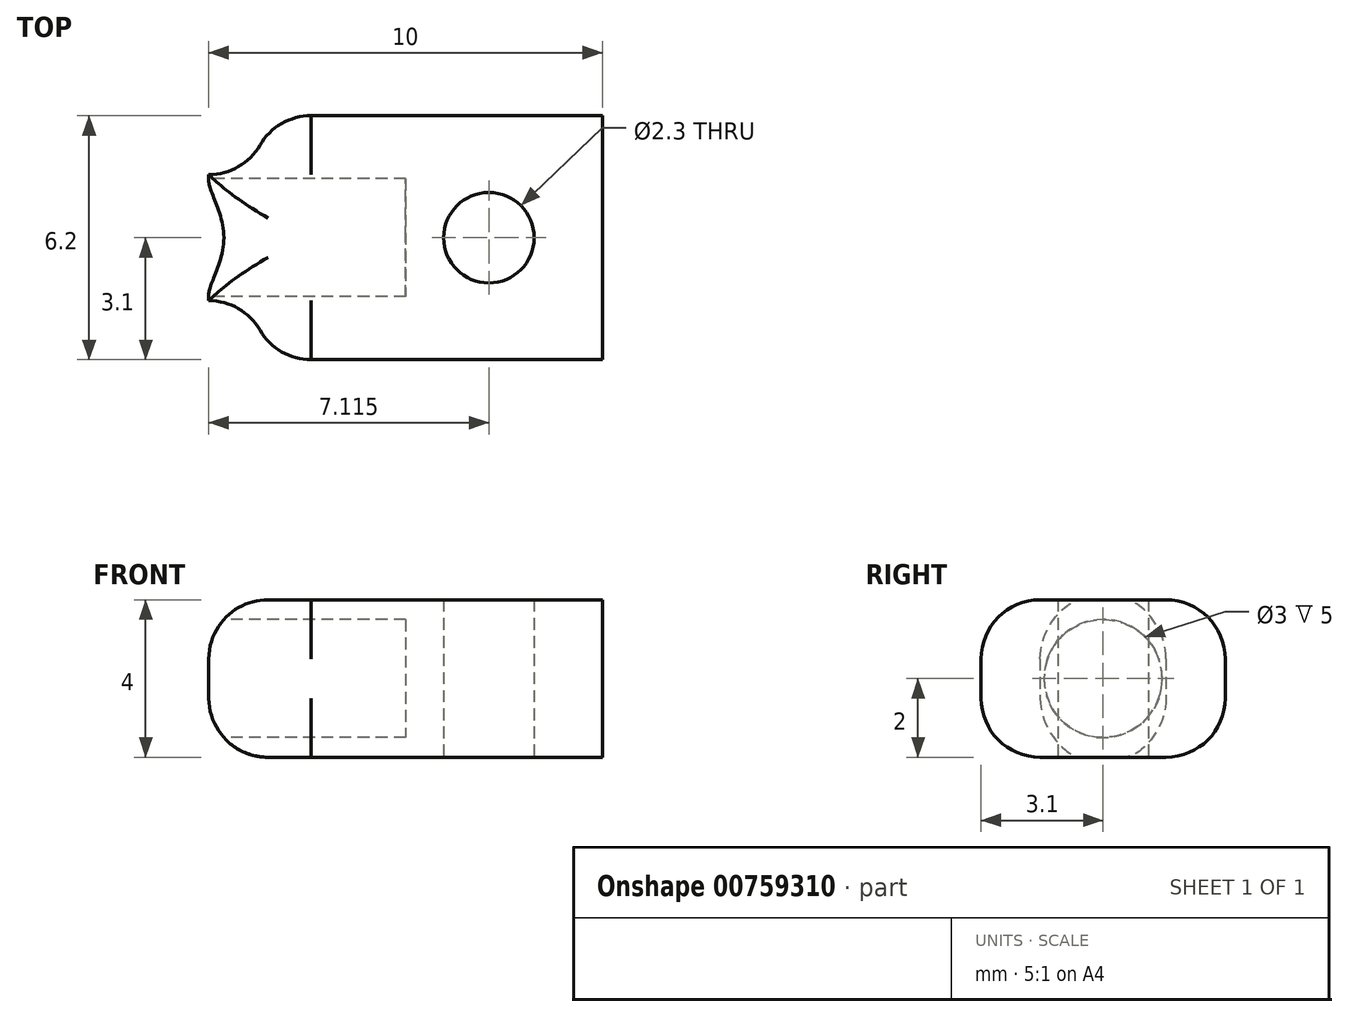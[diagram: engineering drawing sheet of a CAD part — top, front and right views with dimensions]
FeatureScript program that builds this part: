
annotation { "Feature Type Name" : "Feature", "Feature Type Description" : "" }
export const myFeature = defineFeature(function(context is Context, id is Id, definition is map)
    precondition{}
    {
        {
            var Q0;
            Q0=qCreatedBy(makeId("Top.planeOp"),FACE);
            var sketch = newSketch(context, id + "F0", { "sketchPlane" : qUnion([Q0])});
            skLineSegment(sketch, "E0.bottom", {"start": v(-3.5, 3.1) * mm, "end": v(5, 3.1) * mm});
            skLineSegment(sketch, "E0.top", {"start": v(-3.5, -3.1) * mm, "end": v(5, -3.1) * mm});
            skLineSegment(sketch, "E0.left", {"start": v(-5, 1.6) * mm, "end": v(-5, -1.6) * mm});
            skLineSegment(sketch, "E0.right", {"start": v(5, 3.1) * mm, "end": v(5, -3.1) * mm});
            skPoint(sketch, "E0.middle", {"position": v(0, 0) * mm});
            skArc(sketch, "E1", {"start": v(-3.5, -3.1) * mm, "mid": v(-3.94, -2.04) * mm, "end": v(-5, -1.6) * mm});
            skArc(sketch, "E2", {"start": v(-5, 1.6) * mm, "mid": v(-3.94, 2.04) * mm, "end": v(-3.5, 3.1) * mm});
            skLineSegment(sketch, "E3", {"start": v(0.97, 0) * mm, "end": v(1.15, 0) * mm});
            skCircle(sketch, "E4", {"center": v(2.12, 0) * mm, "radius": 1.15 * mm});
            skSolve(sketch);
        }
        {
            var Q0;
            Q0 = qSketchRegion(id + "F0", true);
            extrude(context, id + "F1", {"entities" : qUnion([Q0]), "depth" : 4 * mm, "offsetDistance" : 25 * mm});
        }
        {
            var Q0;
            Q0=makeQuery(id+"F1.opExtrude","SWEPT_FACE",FACE,{"disambiguationData":[OSD([sQuery(id+"F0.wireOp",EDGE,"E0.left")])]});
            var sketch = newSketch(context, id + "F2", { "sketchPlane" : qUnion([Q0])});
            skCircle(sketch, "E5", {"center": v(0, 2) * mm, "radius": 1.5 * mm});
            skPoint(sketch, "E6.trimOffspring.end.orphan", {"position": v(0, 4) * mm});
            skPoint(sketch, "E7.start.orphan", {"position": v(-1.6, 2) * mm});
            skPoint(sketch, "E8.trimOffspring.end.orphan", {"position": v(1.6, 2) * mm});
            skSolve(sketch);
        }
        {
            var Q0;
            Q0=makeQuery(id+"F2.imprint","IMPRINT",FACE,{"disambiguationData":[TD([[makeQuery(id+"F2.imprint","IMPRINT",EDGE,{"derivedFrom":sQuery(id+"F2.wireOp",EDGE,"E5")}),1.0]])]});
            extrude(context, id + "F3", {"entities" : qUnion([Q0]), "operationType" : NewBodyOperationType.REMOVE, "oppositeDirection" : true, "depth" : 5 * mm, "offsetDistance" : 25 * mm});
        }
        {
            var Q0;
            Q0=makeQuery(id+"F1.opExtrude","CAP_EDGE",EDGE,{"disambiguationData":[OSD([sQuery(id+"F0.wireOp",EDGE,"E0.top")])],"isStart":false});
            var Q1;
            Q1=makeQuery(id+"F1.opExtrude","CAP_EDGE",EDGE,{"disambiguationData":[OSD([sQuery(id+"F0.wireOp",EDGE,"E0.top")])],"isStart":true});
            var Q2;
            Q2=makeQuery(id+"F1.opExtrude","CAP_EDGE",EDGE,{"disambiguationData":[OSD([sQuery(id+"F0.wireOp",EDGE,"E0.bottom")])],"isStart":false});
            var Q3;
            Q3=makeQuery(id+"F1.opExtrude","CAP_EDGE",EDGE,{"disambiguationData":[OSD([sQuery(id+"F0.wireOp",EDGE,"E0.bottom")])],"isStart":true});
            fillet(context, id + "F4", {"entities" : qUnion([Q0, Q1, Q2, Q3]), "radius" : 1.5 * mm, "tangentPropagation" : true, "allowEdgeOverflow" : false});
        }
        {
            var Q0;
            Q0=makeQuery(id+"F1.opExtrude","CAP_EDGE",EDGE,{"disambiguationData":[OSD([sQuery(id+"F0.wireOp",EDGE,"E0.left")])],"isStart":false});
            var Q1;
            Q1=makeQuery(id+"F1.opExtrude","CAP_EDGE",EDGE,{"disambiguationData":[OSD([sQuery(id+"F0.wireOp",EDGE,"E0.left")])],"isStart":true});
            var Q2;
            Q2=makeQuery(id+"F4.opFillet","BLEND_EDGE",EDGE,{"blendedFrom":[makeQuery(id+"F1.opExtrude","CAP_EDGE",EDGE,{"disambiguationData":[OSD([sQuery(id+"F0.wireOp",EDGE,"E0.top")])],"isStart":false}),makeQuery(id+"F1.opExtrude","SWEPT_FACE",FACE,{"disambiguationData":[OSD([sQuery(id+"F0.wireOp",EDGE,"E1")])]})],"blendedInto":[makeQuery(id+"F1.opExtrude","SWEPT_FACE",FACE,{"disambiguationData":[OSD([sQuery(id+"F0.wireOp",EDGE,"E1")])]})]});
            var Q3;
            Q3=makeQuery(id+"F4.opFillet","BLEND_EDGE",EDGE,{"blendedFrom":[makeQuery(id+"F1.opExtrude","CAP_EDGE",EDGE,{"disambiguationData":[OSD([sQuery(id+"F0.wireOp",EDGE,"E0.bottom")])],"isStart":false}),makeQuery(id+"F1.opExtrude","SWEPT_FACE",FACE,{"disambiguationData":[OSD([sQuery(id+"F0.wireOp",EDGE,"E2")])]})],"blendedInto":[makeQuery(id+"F1.opExtrude","SWEPT_FACE",FACE,{"disambiguationData":[OSD([sQuery(id+"F0.wireOp",EDGE,"E2")])]})]});
            fillet(context, id + "F5", {"entities" : qUnion([Q0, Q1, Q2, Q3]), "radius" : 1.5 * mm, "tangentPropagation" : true, "allowEdgeOverflow" : false});
        }
    });
